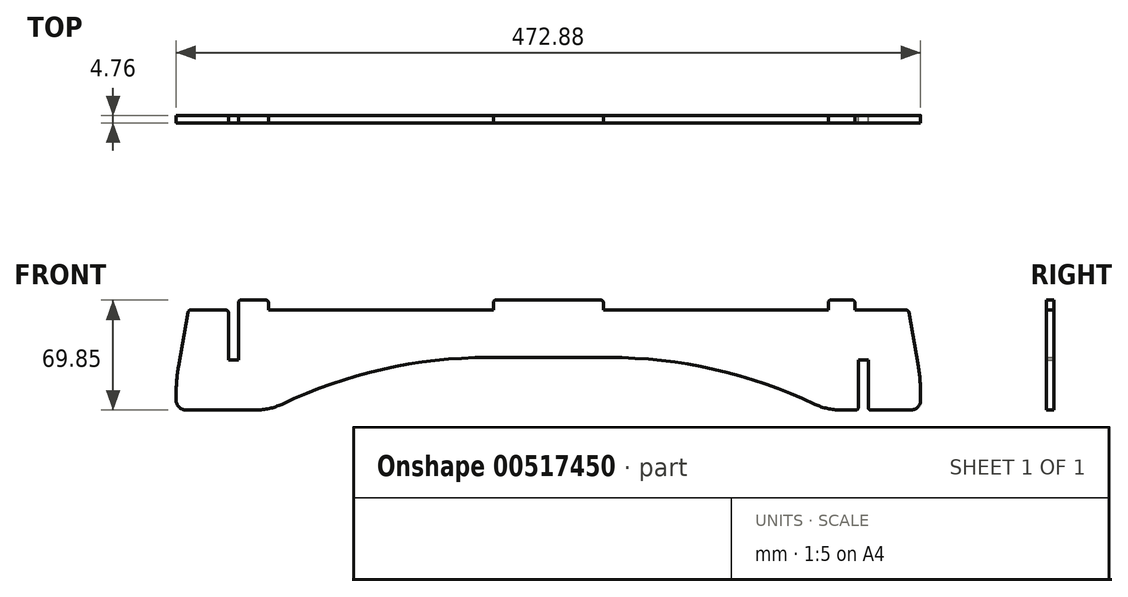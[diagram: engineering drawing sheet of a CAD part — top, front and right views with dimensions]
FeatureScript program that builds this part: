
annotation { "Feature Type Name" : "Feature", "Feature Type Description" : "" }
export const myFeature = defineFeature(function(context is Context, id is Id, definition is map)
    precondition{}
    {
        {
            var Q0;
            Q0=qCreatedBy(makeId("Front.planeOp"),FACE);
            var sketch = newSketch(context, id + "F0", { "sketchPlane" : qUnion([Q0])});
            skLineSegment(sketch, "E0.bottom", {"start": v(-227.27, 0) * mm, "end": v(-204.79, 0) * mm});
            skLineSegment(sketch, "E0.top", {"start": v(-230.09, -63.5) * mm, "end": v(-185.64, -63.5) * mm});
            skLineSegment(sketch, "E0.left", {"start": v(-228.83, -1.31) * mm, "end": v(-234.9, -35.7) * mm});
            skLineSegment(sketch, "E1", {"start": v(0, 0) * mm, "end": v(0, -63.5) * mm, "construction": true});
            skLineSegment(sketch, "E2", {"start": v(-236.44, -57.15) * mm, "end": v(-236.44, -53.34) * mm});
            skPoint(sketch, "E3.visualSharp", {"position": v(-236.44, -44.45) * mm});
            skArc(sketch, "E3.filletArc", {"start": v(-234.9, -35.7) * mm, "mid": v(-236.05, -44.48) * mm, "end": v(-236.44, -53.34) * mm});
            skLineSegment(sketch, "E4", {"start": v(0, -30.14) * mm, "end": v(-38.1, -30.14) * mm});
            skArc(sketch, "E5", {"start": v(-38.1, -30.14) * mm, "mid": v(-105.33, -37.64) * mm, "end": v(-169.24, -59.8) * mm});
            skPoint(sketch, "E6.visualSharp", {"position": v(-176.75, -63.5) * mm});
            skArc(sketch, "E6.filletArc", {"start": v(-185.64, -63.5) * mm, "mid": v(-177.23, -62.56) * mm, "end": v(-169.24, -59.8) * mm});
            skLineSegment(sketch, "E7.top", {"start": v(-195.26, 6.35) * mm, "end": v(-179.39, 6.35) * mm});
            skLineSegment(sketch, "E7.right", {"start": v(-177.8, 0) * mm, "end": v(-177.8, 4.76) * mm});
            skLineSegment(sketch, "E8.trimOffspring", {"start": v(-177.8, 0) * mm, "end": v(0, 0) * mm});
            skLineSegment(sketch, "E9.top", {"start": v(-203.2, -31.75) * mm, "end": v(-196.85, -31.75) * mm});
            skLineSegment(sketch, "E9.left", {"start": v(-203.2, -1.59) * mm, "end": v(-203.2, -31.75) * mm});
            skLineSegment(sketch, "E9.right", {"start": v(-196.85, 4.76) * mm, "end": v(-196.85, -31.75) * mm});
            skPoint(sketch, "E10.visualSharp", {"position": v(-236.44, -63.5) * mm});
            skArc(sketch, "E10.filletArc", {"start": v(-236.44, -57.15) * mm, "mid": v(-234.58, -61.64) * mm, "end": v(-230.09, -63.5) * mm});
            skLineSegment(sketch, "E11.MirrorCS", {"start": v(203.2, -31.75) * mm, "end": v(196.85, -31.75) * mm});
            skLineSegment(sketch, "E12.MirrorCS", {"start": v(177.8, 0) * mm, "end": v(177.8, 4.76) * mm});
            skLineSegment(sketch, "E13.MirrorCS", {"start": v(194.67, 0) * mm, "end": v(194.67, 4.76) * mm});
            skArc(sketch, "E14.MirrorCS", {"start": v(185.64, -63.5) * mm, "mid": v(177.23, -62.56) * mm, "end": v(169.24, -59.8) * mm});
            skArc(sketch, "E15.MirrorCS", {"start": v(236.44, -57.15) * mm, "mid": v(234.58, -61.64) * mm, "end": v(230.09, -63.5) * mm});
            skArc(sketch, "E16.MirrorCS", {"start": v(234.9, -35.7) * mm, "mid": v(236.05, -44.48) * mm, "end": v(236.44, -53.34) * mm});
            skLineSegment(sketch, "E17.MirrorCS", {"start": v(236.44, -57.15) * mm, "end": v(236.44, -53.34) * mm});
            skLineSegment(sketch, "E18.MirrorCS", {"start": v(227.27, 0) * mm, "end": v(194.67, 0) * mm});
            skPoint(sketch, "E19.MirrorP", {"position": v(236.44, -44.45) * mm});
            skLineSegment(sketch, "E20.MirrorCS", {"start": v(228.83, -1.31) * mm, "end": v(234.9, -35.7) * mm});
            skLineSegment(sketch, "E21.MirrorCS", {"start": v(230.09, -63.5) * mm, "end": v(204.79, -63.5) * mm});
            skPoint(sketch, "E22.MirrorP", {"position": v(236.44, -63.5) * mm});
            skLineSegment(sketch, "E23.MirrorCS", {"start": v(193.08, 6.35) * mm, "end": v(179.39, 6.35) * mm});
            skArc(sketch, "E24.MirrorCS", {"start": v(38.1, -30.14) * mm, "mid": v(105.33, -37.64) * mm, "end": v(169.24, -59.8) * mm});
            skLineSegment(sketch, "E25.MirrorCS", {"start": v(177.8, 0) * mm, "end": v(0, 0) * mm});
            skPoint(sketch, "E26.MirrorP", {"position": v(176.75, -63.5) * mm});
            skLineSegment(sketch, "E27.MirrorCS", {"start": v(0, -30.14) * mm, "end": v(38.1, -30.14) * mm});
            skLineSegment(sketch, "E28", {"start": v(196.85, -31.75) * mm, "end": v(196.85, -61.91) * mm});
            skLineSegment(sketch, "E29", {"start": v(203.2, -61.91) * mm, "end": v(203.2, -31.75) * mm});
            skLineSegment(sketch, "E30.trimOffspring", {"start": v(195.26, -63.5) * mm, "end": v(185.64, -63.5) * mm});
            skLineSegment(sketch, "E31", {"start": v(34.92, 0) * mm, "end": v(34.92, 4.76) * mm});
            skLineSegment(sketch, "E32", {"start": v(33.34, 6.35) * mm, "end": v(0, 6.35) * mm});
            skLineSegment(sketch, "E33", {"start": v(0, 6.35) * mm, "end": v(-33.34, 6.35) * mm});
            skLineSegment(sketch, "E34", {"start": v(-34.93, 4.76) * mm, "end": v(-34.93, 0) * mm});
            skArc(sketch, "E35.filletArc", {"start": v(-195.26, 6.35) * mm, "mid": v(-196.39, 5.89) * mm, "end": v(-196.85, 4.76) * mm});
            skPoint(sketch, "E36.visualSharp", {"position": v(-177.8, 6.35) * mm});
            skArc(sketch, "E36.filletArc", {"start": v(-177.8, 4.76) * mm, "mid": v(-178.26, 5.89) * mm, "end": v(-179.39, 6.35) * mm});
            skPoint(sketch, "E37.visualSharp", {"position": v(-34.93, 6.35) * mm});
            skArc(sketch, "E37.filletArc", {"start": v(-33.34, 6.35) * mm, "mid": v(-34.46, 5.89) * mm, "end": v(-34.93, 4.76) * mm});
            skPoint(sketch, "E38.visualSharp", {"position": v(34.92, 6.35) * mm});
            skArc(sketch, "E38.filletArc", {"start": v(34.92, 4.76) * mm, "mid": v(34.46, 5.89) * mm, "end": v(33.34, 6.35) * mm});
            skPoint(sketch, "E39.visualSharp", {"position": v(177.8, 6.35) * mm});
            skArc(sketch, "E39.filletArc", {"start": v(179.39, 6.35) * mm, "mid": v(178.26, 5.89) * mm, "end": v(177.8, 4.76) * mm});
            skPoint(sketch, "E40.visualSharp", {"position": v(194.67, 6.35) * mm});
            skArc(sketch, "E40.filletArc", {"start": v(194.67, 4.76) * mm, "mid": v(194.2, 5.89) * mm, "end": v(193.08, 6.35) * mm});
            skPoint(sketch, "E41.visualSharp", {"position": v(228.6, 0) * mm});
            skArc(sketch, "E41.filletArc", {"start": v(228.83, -1.31) * mm, "mid": v(228.29, -0.37) * mm, "end": v(227.27, 0) * mm});
            skPoint(sketch, "E42.visualSharp", {"position": v(196.85, -63.5) * mm});
            skArc(sketch, "E42.filletArc", {"start": v(195.26, -63.5) * mm, "mid": v(196.39, -63.04) * mm, "end": v(196.85, -61.91) * mm});
            skPoint(sketch, "E43.visualSharp", {"position": v(203.2, -63.5) * mm});
            skArc(sketch, "E43.filletArc", {"start": v(203.2, -61.91) * mm, "mid": v(203.66, -63.04) * mm, "end": v(204.79, -63.5) * mm});
            skPoint(sketch, "E44.visualSharp", {"position": v(-203.2, 0) * mm});
            skArc(sketch, "E44.filletArc", {"start": v(-203.2, -1.59) * mm, "mid": v(-203.66, -0.46) * mm, "end": v(-204.79, 0) * mm});
            skPoint(sketch, "E45.visualSharp", {"position": v(-228.6, 0) * mm});
            skArc(sketch, "E45.filletArc", {"start": v(-227.27, 0) * mm, "mid": v(-228.29, -0.37) * mm, "end": v(-228.83, -1.31) * mm});
            skPoint(sketch, "E46", {"position": v(-200.03, -31.75) * mm});
            skPoint(sketch, "E47", {"position": v(200.03, -31.75) * mm});
            skSolve(sketch);
        }
        {
            var Q0;
            Q0 = qSketchRegion(id + "F0", true);
            extrude(context, id + "F1", {"entities" : qUnion([Q0]), "depth" : 4.76 * mm, "offsetDistance" : 25.4 * mm});
        }
    });
